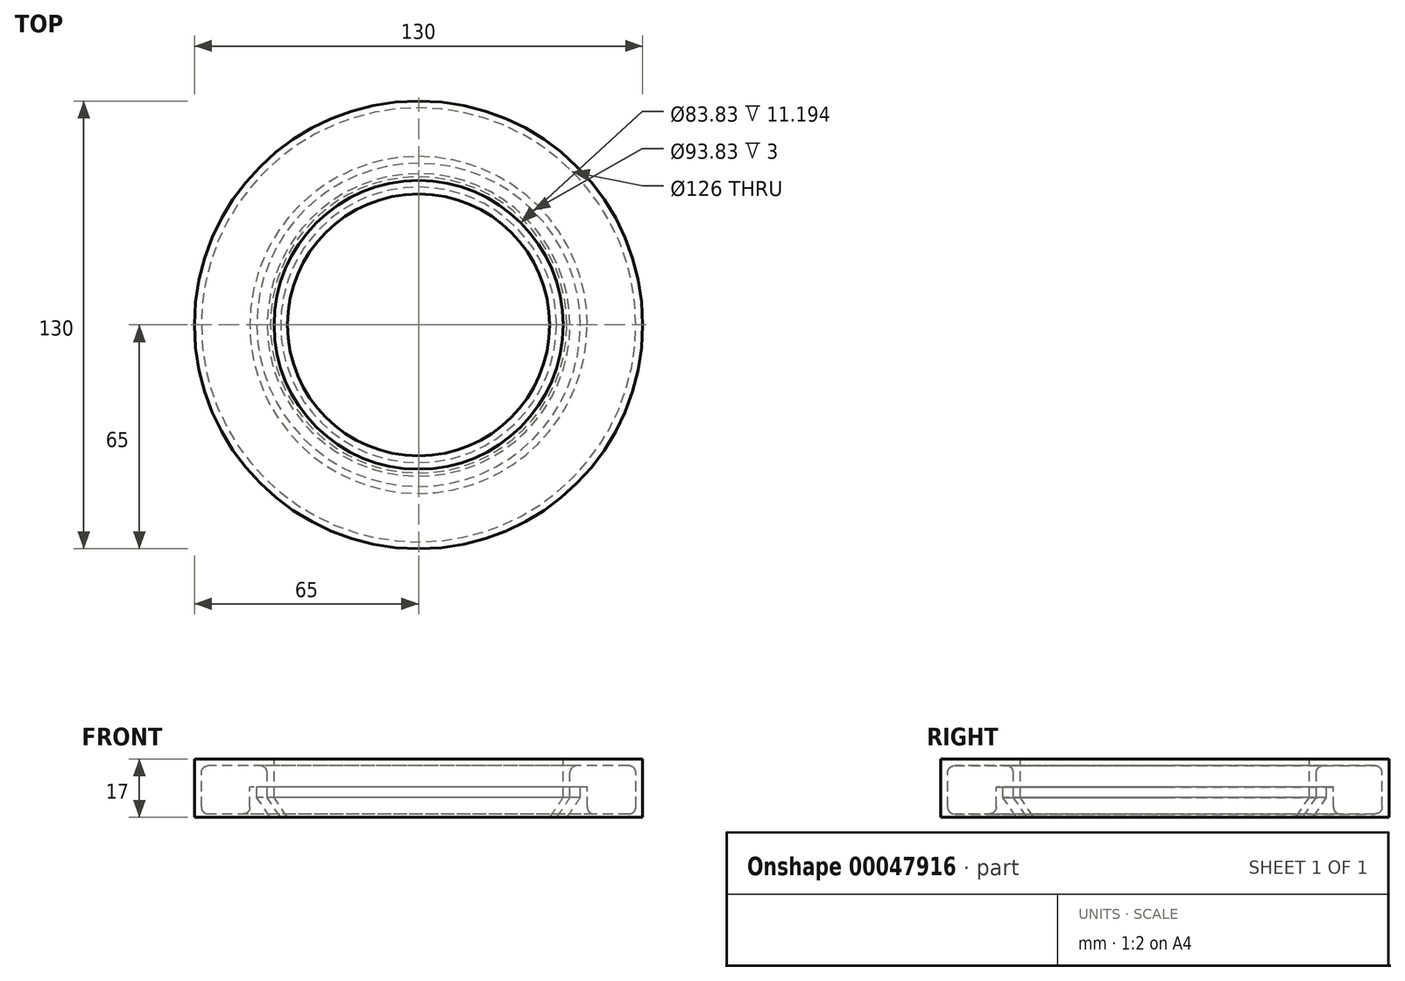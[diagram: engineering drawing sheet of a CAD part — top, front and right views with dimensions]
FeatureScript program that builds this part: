
annotation { "Feature Type Name" : "Feature", "Feature Type Description" : "" }
export const myFeature = defineFeature(function(context is Context, id is Id, definition is map)
    precondition{}
    {
        {
            var Q0;
            Q0=qCreatedBy(makeId("Front.planeOp"),FACE);
            var sketch = newSketch(context, id + "F0", { "sketchPlane" : qUnion([Q0])});
            skLineSegment(sketch, "E0", {"start": v(0, 73.35) * mm, "end": v(0, -66.12) * mm});
            skSolve(sketch);
        }
        {
            var Q0;
            Q0=qCreatedBy(makeId("Front.planeOp"),FACE);
            var sketch = newSketch(context, id + "F1", { "sketchPlane" : qUnion([Q0])});
            skLineSegment(sketch, "E1", {"start": v(-38, 0) * mm, "end": v(-41.92, 5.8) * mm});
            skLineSegment(sketch, "E2", {"start": v(-41.92, 5.8) * mm, "end": v(-41.92, 17) * mm});
            skLineSegment(sketch, "E3", {"start": v(-40, 0) * mm, "end": v(-43.92, 5.8) * mm});
            skLineSegment(sketch, "E4", {"start": v(-40, 0) * mm, "end": v(-38, 0) * mm});
            skLineSegment(sketch, "E5", {"start": v(-43.92, 5.8) * mm, "end": v(-43.92, 13) * mm});
            skLineSegment(sketch, "E6", {"start": v(-43, 0) * mm, "end": v(-46.92, 5.8) * mm});
            skLineSegment(sketch, "E7", {"start": v(-46.92, 5.8) * mm, "end": v(-46.92, 8.8) * mm});
            skLineSegment(sketch, "E8", {"start": v(-43, 0) * mm, "end": v(-65, 0) * mm});
            skLineSegment(sketch, "E9", {"start": v(-65, 0) * mm, "end": v(-65, 17) * mm});
            skLineSegment(sketch, "E10", {"start": v(-46.92, 8.8) * mm, "end": v(-48.92, 8.8) * mm});
            skLineSegment(sketch, "E11", {"start": v(-48.92, 8.8) * mm, "end": v(-48.92, 3) * mm});
            skLineSegment(sketch, "E12", {"start": v(-50.92, 1) * mm, "end": v(-61, 1) * mm});
            skLineSegment(sketch, "E13", {"start": v(-65, 17) * mm, "end": v(-41.92, 17) * mm});
            skLineSegment(sketch, "E14", {"start": v(-45.92, 15) * mm, "end": v(-61, 15) * mm});
            skLineSegment(sketch, "E15", {"start": v(-63, 13) * mm, "end": v(-63, 3) * mm});
            skPoint(sketch, "E16.visualSharp", {"position": v(-63, 1) * mm});
            skArc(sketch, "E16.filletArc", {"start": v(-63, 3) * mm, "mid": v(-62.41, 1.59) * mm, "end": v(-61, 1) * mm});
            skPoint(sketch, "E17.visualSharp", {"position": v(-63, 15) * mm});
            skArc(sketch, "E17.filletArc", {"start": v(-61, 15) * mm, "mid": v(-62.41, 14.41) * mm, "end": v(-63, 13) * mm});
            skPoint(sketch, "E18.visualSharp", {"position": v(-43.92, 15) * mm});
            skArc(sketch, "E18.filletArc", {"start": v(-43.92, 13) * mm, "mid": v(-44.5, 14.41) * mm, "end": v(-45.92, 15) * mm});
            skPoint(sketch, "E19.visualSharp", {"position": v(-48.92, 1) * mm});
            skArc(sketch, "E19.filletArc", {"start": v(-50.92, 1) * mm, "mid": v(-49.5, 1.59) * mm, "end": v(-48.92, 3) * mm});
            skSolve(sketch);
        }
        {
            var Q0;
            Q0 = qSketchRegion(id + "F1", true);
            var Q1;
            Q1=sQuery(id+"F0.wireOp",EDGE,"E0");
            revolve(context, id + "F2", {"entities" : qUnion([Q0]), "axis" : qUnion([Q1]), "revolveType" : RevolveType.FULL});
        }
    });
